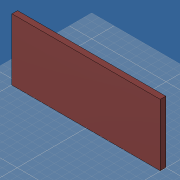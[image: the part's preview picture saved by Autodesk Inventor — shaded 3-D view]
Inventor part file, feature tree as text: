
AUTODESK INVENTOR PART (.ipt)
format: ipt  version: 2019 (Build 230136000, 136)  size: 95,232 bytes
history: native  units: mm
features: extrude x2, other x1, sketch x1
ambient origin geometry x8: Origin, YZ Plane, XZ Plane, XY Plane, X Axis, Y Axis, Z Axis, Center Point
bodies: Volumenkörper1 (feature_tree)
feature tree (4):
  other  "<userpath>\OneDrive\Dokumente\Inventor\Absauganlage\Absauganlage_Params.xlsx"
  sketch  "Skizze1"  dims[d0=398.0mm d1=166.0mm d2=8.0mm d3=17.0mm d4=15.0mm d5=0.0mm d6=6.0mm d7=0.0mm]
  extrude  "Extrusion1"  Depth=166.0mm
  extrude  "Extrusion2"  Depth=8.0mm
